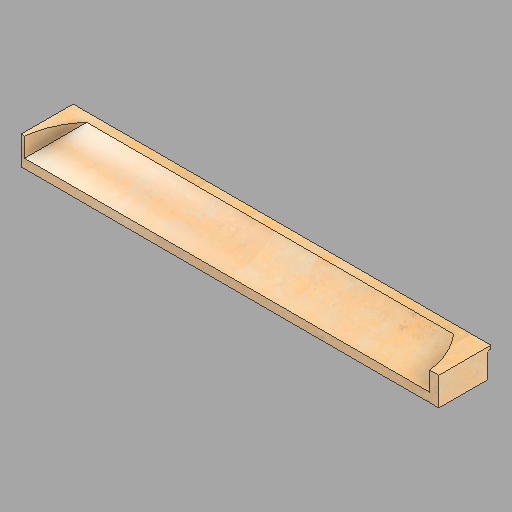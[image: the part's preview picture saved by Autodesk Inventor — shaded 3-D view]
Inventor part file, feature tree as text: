
AUTODESK INVENTOR PART (.ipt)
format: ipt  version: 2022.2 (Build 262287010, 287A)  size: 210,432 bytes
history: native  units: in
note: dims shown in document units (in); Inventor stores cm internally (conversion verified against a paired STEP export)
features: revolve x2, other x1, direct_edit x1
ambient origin geometry x8: Origin, YZ Plane, XZ Plane, XY Plane, X Axis, Y Axis, Z Axis, Center Point
bodies: Solid1 (feature_tree)
feature tree (4):
  other  "Head (L)"
  direct_edit  "Direct Edit1"
  revolve  "Rotate1"  [1 undecoded]
  revolve  "Rotate2"  [1 undecoded]
note: 2 required parameter values undecoded (feature->parameter linkage not recoverable at this tier; creation-order binding heuristic only, values carry confidence <= 0.55)
